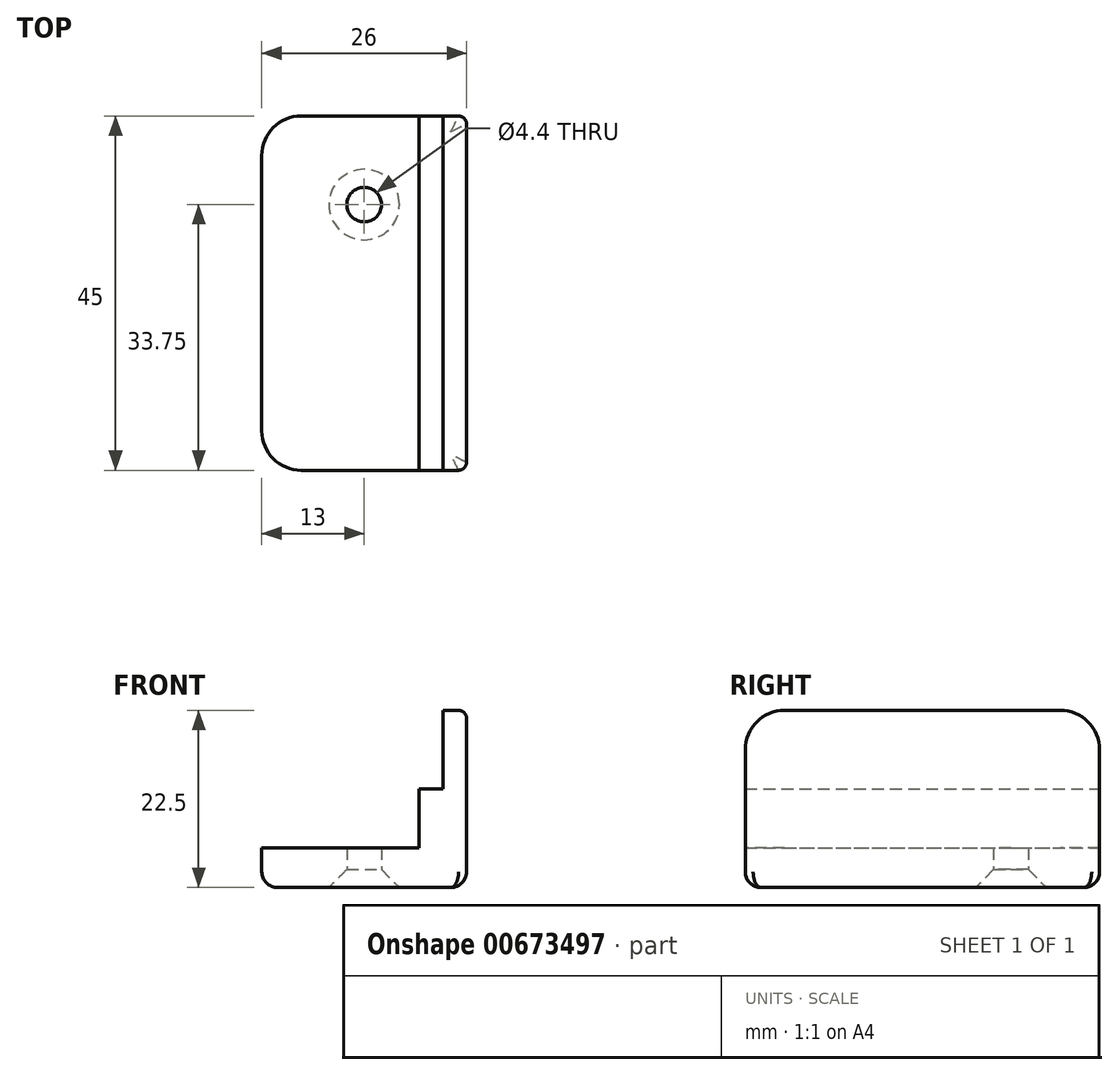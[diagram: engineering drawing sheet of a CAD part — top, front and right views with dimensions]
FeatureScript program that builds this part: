
annotation { "Feature Type Name" : "Feature", "Feature Type Description" : "" }
export const myFeature = defineFeature(function(context is Context, id is Id, definition is map)
    precondition{}
    {
        {
            var Q0;
            Q0=qCreatedBy(makeId("Front.planeOp"),FACE);
            var sketch = newSketch(context, id + "F0", { "sketchPlane" : qUnion([Q0])});
            skLineSegment(sketch, "E0", {"start": v(0, 22.5) * mm, "end": v(0, 0) * mm});
            skLineSegment(sketch, "E1", {"start": v(0, 0) * mm, "end": v(-26, 0) * mm});
            skLineSegment(sketch, "E2", {"start": v(-26, 0) * mm, "end": v(-26, 5) * mm});
            skLineSegment(sketch, "E3", {"start": v(-26, 5) * mm, "end": v(-6, 5) * mm});
            skLineSegment(sketch, "E4", {"start": v(-6, 5) * mm, "end": v(-6, 12.5) * mm});
            skLineSegment(sketch, "E5", {"start": v(-6, 12.5) * mm, "end": v(-3, 12.5) * mm});
            skLineSegment(sketch, "E6", {"start": v(-3, 12.5) * mm, "end": v(-3, 22.5) * mm});
            skLineSegment(sketch, "E7", {"start": v(-3, 22.5) * mm, "end": v(0, 22.5) * mm});
            skSolve(sketch);
        }
        {
            var Q0;
            Q0 = qSketchRegion(id + "F0", true);
            extrude(context, id + "F1", {"entities" : qUnion([Q0]), "endBound" : BoundingType.SYMMETRIC, "depth" : 45 * mm, "offsetDistance" : 25 * mm});
        }
        {
            var Q0;
            Q0=makeQuery(id+"F1.opExtrude","SWEPT_FACE",FACE,{"disambiguationData":[OSD([sQuery(id+"F0.wireOp",EDGE,"E1")])]});
            var sketch = newSketch(context, id + "F2", { "sketchPlane" : qUnion([Q0])});
            skLineSegment(sketch, "E8", {"start": v(-26, 0) * mm, "end": v(0, 0) * mm, "construction": true});
            skPoint(sketch, "E9", {"position": v(-13, -11.25) * mm});
            skSolve(sketch);
        }
        {
            var Q0;
            Q0=sQuery(id+"F2.wireOp",VERTEX,"E9");
            var Q1;
            Q1=makeQuery(id+"F1.opExtrude","SWEPT_BODY",BODY,{"disambiguationData":[OSD([sQuery(id+"F0.wireOp",EDGE,"E0"),sQuery(id+"F0.wireOp",EDGE,"E1"),sQuery(id+"F0.wireOp",EDGE,"E2"),sQuery(id+"F0.wireOp",EDGE,"E3"),sQuery(id+"F0.wireOp",EDGE,"E4"),sQuery(id+"F0.wireOp",EDGE,"E5"),sQuery(id+"F0.wireOp",EDGE,"E6"),sQuery(id+"F0.wireOp",EDGE,"E7")])]});
            hole(context, id + "F3", {"style" : HoleStyle.C_SINK, "endStyle" : HoleEndStyle.THROUGH, "standardTappedOrClearance" : lookupTablePath({ "standard" : "ISO", "fit" : "Normal", "size" : "M4", "type" : "Clearance" }), "standardBlindInLast" : lookupTablePath({ "fit" : "Standard", "standard" : "ISO", "size" : "M4", "type" : "Clearance" }), "holeDiameter" : 4.4 * mm, "cSinkDiameter" : 8.96 * mm, "cSinkAngle" : 90 * degree, "majorDiameter" : 5 * mm, "isTappedThrough" : true, "tappedDepth" : 12 * mm, "tapClearance" : 3, "locations" : qUnion([Q0]), "scope" : qUnion([Q1])});
        }
        {
            var Q0;
            Q0=makeQuery(id+"F1.opExtrude","CAP_EDGE",EDGE,{"disambiguationData":[OSD([sQuery(id+"F0.wireOp",EDGE,"E2")])],"isStart":true});
            var Q1;
            Q1=makeQuery(id+"F1.opExtrude","CAP_EDGE",EDGE,{"disambiguationData":[OSD([sQuery(id+"F0.wireOp",EDGE,"E2")])],"isStart":false});
            var Q2;
            Q2=makeQuery(id+"F1.opExtrude","CAP_EDGE",EDGE,{"disambiguationData":[OSD([sQuery(id+"F0.wireOp",EDGE,"E7")])],"isStart":false});
            var Q3;
            Q3=makeQuery(id+"F1.opExtrude","CAP_EDGE",EDGE,{"disambiguationData":[OSD([sQuery(id+"F0.wireOp",EDGE,"E7")])],"isStart":true});
            fillet(context, id + "F4", {"entities" : qUnion([Q0, Q1, Q2, Q3]), "radius" : 5 * mm, "tangentPropagation" : true, "allowEdgeOverflow" : false});
        }
        {
            var Q0;
            Q0=makeQuery(id+"F1.opExtrude","CAP_EDGE",EDGE,{"disambiguationData":[OSD([sQuery(id+"F0.wireOp",EDGE,"E0")])],"isStart":true});
            fillet(context, id + "F5", {"entities" : qUnion([Q0]), "radius" : 1 * mm, "tangentPropagation" : true, "allowEdgeOverflow" : false});
        }
        {
            var Q0;
            Q0=makeQuery(id+"F1.opExtrude","SWEPT_EDGE",EDGE,{"disambiguationData":[OSD([sQuery(id+"F0.wireOp",EDGE,"E1"),sQuery(id+"F0.wireOp",EDGE,"E2")])]});
            fillet(context, id + "F6", {"entities" : qUnion([Q0]), "radius" : 2 * mm, "tangentPropagation" : true, "allowEdgeOverflow" : false});
        }
    });
